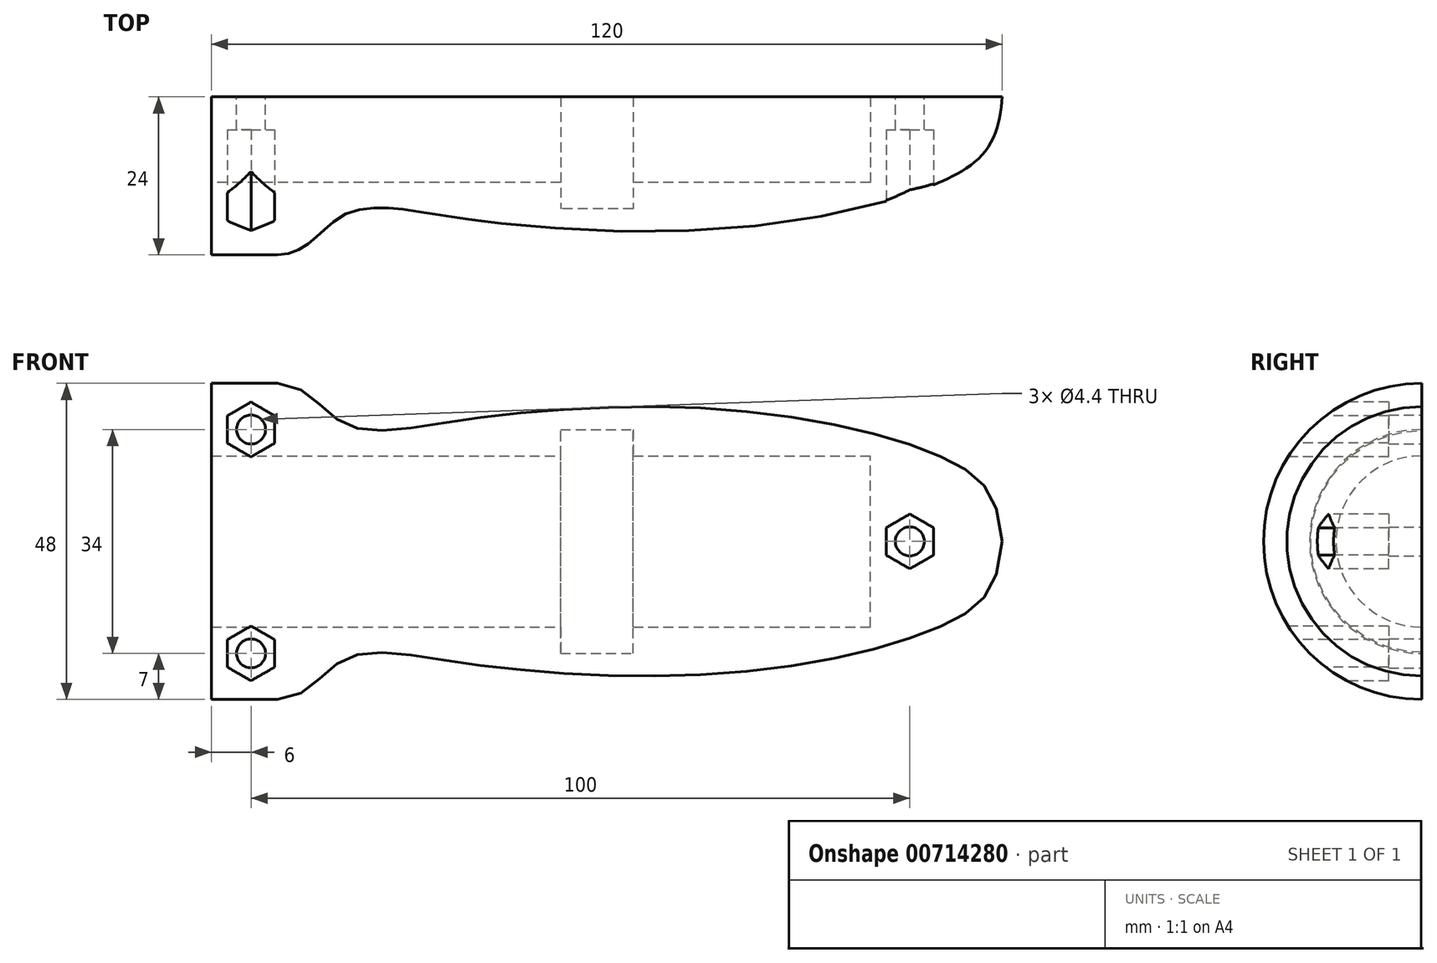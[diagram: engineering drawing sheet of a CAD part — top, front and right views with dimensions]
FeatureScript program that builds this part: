
annotation { "Feature Type Name" : "Feature", "Feature Type Description" : "" }
export const myFeature = defineFeature(function(context is Context, id is Id, definition is map)
    precondition{}
    {
        {
            var Q0;
            Q0=qCreatedBy(makeId("Front.planeOp"),FACE);
            var sketch = newSketch(context, id + "F0", { "sketchPlane" : qUnion([Q0])});
            skLineSegment(sketch, "E0", {"start": v(0, 0) * mm, "end": v(100, 0) * mm, "construction": true});
            skLineSegment(sketch, "E1", {"start": v(0, 13) * mm, "end": v(53, 13) * mm});
            skLineSegment(sketch, "E2", {"start": v(53, 13) * mm, "end": v(53, 17) * mm});
            skLineSegment(sketch, "E3", {"start": v(53, 17) * mm, "end": v(64, 17) * mm});
            skLineSegment(sketch, "E4", {"start": v(64, 17) * mm, "end": v(64, 13) * mm});
            skLineSegment(sketch, "E5", {"start": v(64, 13) * mm, "end": v(100, 13) * mm});
            skLineSegment(sketch, "E6", {"start": v(100, 13) * mm, "end": v(100, 0) * mm});
            skLineSegment(sketch, "E7", {"start": v(100, 0) * mm, "end": v(120, 0) * mm});
            skLineSegment(sketch, "E8", {"start": v(0, 13) * mm, "end": v(0, 24) * mm});
            skLineSegment(sketch, "E9", {"start": v(0, 24) * mm, "end": v(10, 24) * mm});
            skFitSpline(sketch, "E10", {"points": [v(10, 24) * mm, v(19.95, 18) * mm, v(36.95, 18.27) * mm, v(77.98, 20.01) * mm, v(111.53, 12.51) * mm, v(120, 0) * mm], "startDerivative": vector(95.58, 0) * mm, "endDerivative": vector(7.27, -135.02) * mm});
            skSolve(sketch);
        }
        {
            var Q0;
            Q0=makeQuery(id+"F0.imprint","IMPRINT",FACE,{"disambiguationData":[TD([[makeQuery(id+"F0.imprint","IMPRINT",EDGE,{"derivedFrom":sQuery(id+"F0.wireOp",EDGE,"E1")}),1.0]])]});
            var Q1;
            Q1=sQuery(id+"F0.wireOp",EDGE,"E0");
            revolve(context, id + "F1", {"surfaceOperationType" : NewSurfaceOperationType.NEW, "entities" : qUnion([Q0]), "axis" : qUnion([Q1]), "revolveType" : RevolveType.ONE_DIRECTION, "angle" : 180 * degree});
        }
        {
            var Q0;
            Q0=qCreatedBy(makeId("Front.planeOp"),FACE);
            var sketch = newSketch(context, id + "F2", { "sketchPlane" : qUnion([Q0])});
            skLineSegment(sketch, "E11", {"start": v(6, 17) * mm, "end": v(6, -17) * mm, "construction": true});
            skLineSegment(sketch, "E12", {"start": v(6, 0) * mm, "end": v(106, 0) * mm, "construction": true});
            skSolve(sketch);
        }
        {
            var Q0;
            Q0=sQuery(id+"F2.wireOp",VERTEX,"E11.start");
            var Q1;
            Q1=sQuery(id+"F2.wireOp",VERTEX,"E11.end");
            var Q2;
            Q2=sQuery(id+"F2.wireOp",VERTEX,"E12.end");
            var Q3;
            Q3=makeQuery(id+"F1.opRevolve","SWEPT_BODY",BODY,{"disambiguationData":[OSD([sQuery(id+"F0.wireOp",EDGE,"E1"),sQuery(id+"F0.wireOp",EDGE,"E2"),sQuery(id+"F0.wireOp",EDGE,"E3"),sQuery(id+"F0.wireOp",EDGE,"E4"),sQuery(id+"F0.wireOp",EDGE,"E5"),sQuery(id+"F0.wireOp",EDGE,"E6"),sQuery(id+"F0.wireOp",EDGE,"E7"),sQuery(id+"F0.wireOp",EDGE,"E8"),sQuery(id+"F0.wireOp",EDGE,"E9"),sQuery(id+"F0.wireOp",EDGE,"E10")])]});
            hole(context, id + "F3", {"style" : HoleStyle.SIMPLE, "endStyle" : HoleEndStyle.THROUGH, "oppositeDirection" : true, "holeDiameter" : 4.4 * mm, "majorDiameter" : 5 * mm, "isTappedThrough" : true, "tappedDepth" : 12 * mm, "tapClearance" : 3, "locations" : qUnion([Q0, Q1, Q2]), "scope" : qUnion([Q3])});
        }
        {
            var Q0;
            Q0=makeQuery(id+"F1.opRevolve","SWEPT_EDGE",EDGE,{"disambiguationData":[OSD([sQuery(id+"F0.wireOp",EDGE,"E8"),sQuery(id+"F0.wireOp",EDGE,"E9")])]});
            cPoint(context, id + "F4", {"entities" : qUnion([Q0]), "parameter" : 0.5});
        }
        {
            var Q0;
            Q0=qCreatedBy(makeId("Front.planeOp"),FACE);
            var Q1;
            Q1 = qCreatedBy(id + "F4" ,VERTEX);
            cPlane(context, id + "F5", {"entities" : qUnion([Q0, Q1]), "cplaneType" : CPlaneType.PLANE_POINT, "offset" : 25 * mm, "width" : 150 * mm, "height" : 150 * mm});
        }
        {
            var Q0;
            Q0=qCreatedBy(id+"F5.planeOp",FACE);
            var sketch = newSketch(context, id + "F6", { "sketchPlane" : qUnion([Q0])});
            skCircle(sketch, "E13.0", {"center": v(6, 17) * mm, "radius": 2.2 * mm});
            skCircle(sketch, "E14.0", {"center": v(6, -17) * mm, "radius": 2.2 * mm});
            skCircle(sketch, "E15.0", {"center": v(106, 0) * mm, "radius": 2.2 * mm});
            skCircle(sketch, "E16.cCircle", {"center": v(6, 17) * mm, "radius": 3.6 * mm, "construction": true});
            skLineSegment(sketch, "E16.0", {"start": v(9.6, 19.08) * mm, "end": v(9.6, 14.92) * mm});
            skLineSegment(sketch, "E16.1", {"start": v(9.6, 14.92) * mm, "end": v(6, 12.84) * mm});
            skLineSegment(sketch, "E16.2", {"start": v(6, 12.84) * mm, "end": v(2.4, 14.92) * mm});
            skLineSegment(sketch, "E16.3", {"start": v(2.4, 14.92) * mm, "end": v(2.4, 19.08) * mm});
            skLineSegment(sketch, "E16.4", {"start": v(2.4, 19.08) * mm, "end": v(6, 21.16) * mm});
            skLineSegment(sketch, "E16.5", {"start": v(6, 21.16) * mm, "end": v(9.6, 19.08) * mm});
            skPoint(sketch, "E16.0.midPoint", {"position": v(9.6, 17) * mm});
            skCircle(sketch, "E17.cCircle", {"center": v(6, -17) * mm, "radius": 3.6 * mm, "construction": true});
            skLineSegment(sketch, "E17.0", {"start": v(9.6, -14.92) * mm, "end": v(9.6, -19.08) * mm});
            skLineSegment(sketch, "E17.1", {"start": v(9.6, -19.08) * mm, "end": v(6, -21.16) * mm});
            skLineSegment(sketch, "E17.2", {"start": v(6, -21.16) * mm, "end": v(2.4, -19.08) * mm});
            skLineSegment(sketch, "E17.3", {"start": v(2.4, -19.08) * mm, "end": v(2.4, -14.92) * mm});
            skLineSegment(sketch, "E17.4", {"start": v(2.4, -14.92) * mm, "end": v(6, -12.84) * mm});
            skLineSegment(sketch, "E17.5", {"start": v(6, -12.84) * mm, "end": v(9.6, -14.92) * mm});
            skPoint(sketch, "E17.0.midPoint", {"position": v(9.6, -17) * mm});
            skCircle(sketch, "E18.cCircle", {"center": v(106, 0) * mm, "radius": 3.6 * mm, "construction": true});
            skLineSegment(sketch, "E18.0", {"start": v(109.6, 2.08) * mm, "end": v(109.6, -2.08) * mm});
            skLineSegment(sketch, "E18.1", {"start": v(109.6, -2.08) * mm, "end": v(106, -4.16) * mm});
            skLineSegment(sketch, "E18.2", {"start": v(106, -4.16) * mm, "end": v(102.4, -2.08) * mm});
            skLineSegment(sketch, "E18.3", {"start": v(102.4, -2.08) * mm, "end": v(102.4, 2.08) * mm});
            skLineSegment(sketch, "E18.4", {"start": v(102.4, 2.08) * mm, "end": v(106, 4.16) * mm});
            skLineSegment(sketch, "E18.5", {"start": v(106, 4.16) * mm, "end": v(109.6, 2.08) * mm});
            skPoint(sketch, "E18.0.midPoint", {"position": v(109.6, 0) * mm});
            skSolve(sketch);
        }
        {
            var Q0;
            Q0=makeQuery(id+"F6.imprint","IMPRINT",FACE,{"disambiguationData":[TD([[makeQuery(id+"F6.imprint","IMPRINT",EDGE,{"derivedFrom":sQuery(id+"F6.wireOp",EDGE,"E13.0")}),-1.0]])]});
            var Q1;
            Q1=makeQuery(id+"F6.imprint","IMPRINT",FACE,{"disambiguationData":[TD([[makeQuery(id+"F6.imprint","IMPRINT",EDGE,{"derivedFrom":sQuery(id+"F6.wireOp",EDGE,"E14.0")}),-1.0]])]});
            var Q2;
            Q2=makeQuery(id+"F6.imprint","IMPRINT",FACE,{"disambiguationData":[TD([[makeQuery(id+"F6.imprint","IMPRINT",EDGE,{"derivedFrom":sQuery(id+"F6.wireOp",EDGE,"E15.0")}),-1.0]])]});
            extrude(context, id + "F7", {"entities" : qUnion([Q0, Q1, Q2]), "operationType" : NewBodyOperationType.REMOVE, "oppositeDirection" : true, "depth" : 19 * mm, "offsetDistance" : 25 * mm});
        }
    });
